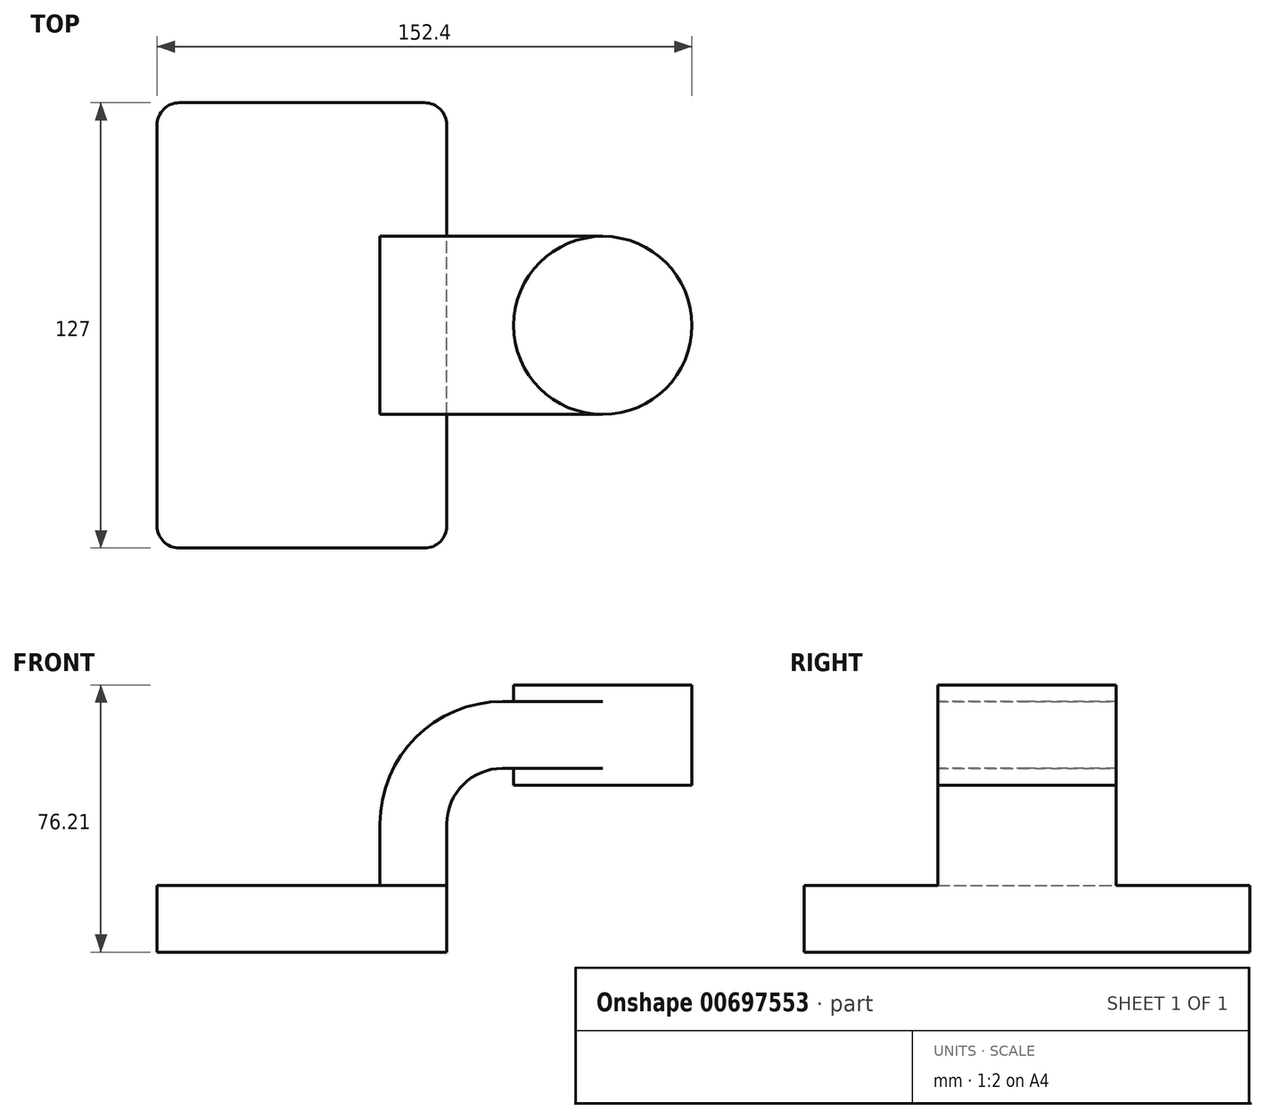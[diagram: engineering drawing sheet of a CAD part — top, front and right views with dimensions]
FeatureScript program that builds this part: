
annotation { "Feature Type Name" : "Feature", "Feature Type Description" : "" }
export const myFeature = defineFeature(function(context is Context, id is Id, definition is map)
    precondition{}
    {
        {
            var Q0;
            Q0=qCreatedBy(makeId("Front.planeOp"),FACE);
            var sketch = newSketch(context, id + "F0", { "sketchPlane" : qUnion([Q0])});
            skLineSegment(sketch, "E0.bottom", {"start": v(-41.28, -9.52) * mm, "end": v(41.28, -9.52) * mm});
            skLineSegment(sketch, "E0.top", {"start": v(-41.28, 9.53) * mm, "end": v(41.28, 9.53) * mm});
            skLineSegment(sketch, "E0.left", {"start": v(-41.28, -9.52) * mm, "end": v(-41.28, 9.53) * mm});
            skLineSegment(sketch, "E0.right", {"start": v(41.28, -9.52) * mm, "end": v(41.28, 9.53) * mm});
            skPoint(sketch, "E0.middle", {"position": v(0, 0) * mm});
            skLineSegment(sketch, "E1.bottom", {"start": v(60.32, 38.1) * mm, "end": v(111.13, 38.1) * mm});
            skLineSegment(sketch, "E1.top", {"start": v(60.32, 66.68) * mm, "end": v(111.12, 66.68) * mm});
            skLineSegment(sketch, "E1.left", {"start": v(60.32, 38.1) * mm, "end": v(60.32, 66.68) * mm});
            skLineSegment(sketch, "E1.right", {"start": v(111.13, 38.1) * mm, "end": v(111.13, 66.68) * mm});
            skPoint(sketch, "E1.middle", {"position": v(85.72, 52.39) * mm});
            skLineSegment(sketch, "E2", {"start": v(41.27, 9.53) * mm, "end": v(41.27, 27) * mm});
            skArc(sketch, "E3", {"start": v(41.27, 27) * mm, "mid": v(45.92, 38.23) * mm, "end": v(57.15, 42.88) * mm});
            skLineSegment(sketch, "E4", {"start": v(57.15, 42.88) * mm, "end": v(85.72, 42.88) * mm});
            skLineSegment(sketch, "E5.0", {"start": v(57.15, 61.93) * mm, "end": v(85.72, 61.93) * mm});
            skArc(sketch, "E5.1", {"start": v(22.22, 27) * mm, "mid": v(32.45, 51.7) * mm, "end": v(57.15, 61.93) * mm});
            skLineSegment(sketch, "E5.2", {"start": v(22.22, 9.53) * mm, "end": v(22.22, 27) * mm});
            skLineSegment(sketch, "E6", {"start": v(85.72, 38.1) * mm, "end": v(85.72, 66.68) * mm});
            skFitSpline(sketch, "E7", {"points": [v(-41.27, 9.52) * mm, v(57.15, 61.93) * mm], "startDerivative": vector(0, 59.37) * mm, "endDerivative": vector(123, 0) * mm});
            skSolve(sketch);
        }
        {
            var Q0;
            Q0=makeQuery(id+"F0.imprint","IMPRINT",FACE,{"disambiguationData":[TD([[makeQuery(id+"F0.imprint","IMPRINT",EDGE,{"derivedFrom":sQuery(id+"F0.wireOp",EDGE,"E0.bottom")}),1.0]])]});
            extrude(context, id + "F1", {"entities" : qUnion([Q0]), "endBound" : BoundingType.SYMMETRIC, "depth" : 127 * mm, "offsetDistance" : 25.4 * mm});
        }
        {
            var Q0;
            {var subQ1=sQuery(id+"F0.wireOp",EDGE,"E2");Q0=makeQuery(id+"F0.imprint","IMPRINT",FACE,{"disambiguationData":[TD([[makeQuery(id+"F0.imprint","IMPRINT",EDGE,{"derivedFrom":subQ1}),1.0]])]});}
            var Q1;
            {var subQ0=sQuery(id+"F0.wireOp",EDGE,"E4");var subQ1=sQuery(id+"F0.wireOp",EDGE,"E1.left");var subQ2=makeQuery(id+"F0.imprint","INTERSECT",VERTEX,{"derivedFrom":[subQ1,subQ0]});Q1=makeQuery(id+"F0.imprint","IMPRINT",FACE,{"disambiguationData":[TD([[makeQuery(id+"F0.imprint","IMPRINT",EDGE,{"disambiguationData":[TD([[subQ2,-1.0]])],"derivedFrom":subQ1}),-1.0]])]});}
            extrude(context, id + "F2", {"entities" : qUnion([Q0, Q1]), "operationType" : NewBodyOperationType.ADD, "endBound" : BoundingType.SYMMETRIC, "depth" : 50.8 * mm, "offsetDistance" : 25.4 * mm});
        }
        {
            var Q0;
            Q0=makeQuery(id+"F0.imprint","IMPRINT",FACE,{"disambiguationData":[TD([[makeQuery(id+"F0.imprint","IMPRINT",EDGE,{"derivedFrom":sQuery(id+"F0.wireOp",EDGE,"E5.1")}),1.0]])]});
            extrude(context, id + "F3", {"entities" : qUnion([Q0]), "operationType" : NewBodyOperationType.ADD, "endBound" : BoundingType.SYMMETRIC, "depth" : 15.88 * mm, "offsetDistance" : 25.4 * mm});
        }
        {
            var Q0;
            {var subQ0=sQuery(id+"F0.wireOp",EDGE,"E1.right");Q0=makeQuery(id+"F0.imprint","IMPRINT",FACE,{"disambiguationData":[TD([[makeQuery(id+"F0.imprint","IMPRINT",EDGE,{"derivedFrom":subQ0}),1.0]])]});}
            var Q1;
            Q1=sQuery(id+"F0.wireOp",EDGE,"E6");
            revolve(context, id + "F4", {"operationType" : NewBodyOperationType.ADD, "entities" : qUnion([Q0]), "axis" : qUnion([Q1]), "revolveType" : RevolveType.FULL});
        }
        {
            var Q0;
            Q0=makeQuery(id+"F1.opExtrude","CAP_EDGE",EDGE,{"disambiguationData":[OSD([sQuery(id+"F0.wireOp",EDGE,"E0.right")])],"isStart":false});
            var Q1;
            Q1=makeQuery(id+"F1.opExtrude","CAP_EDGE",EDGE,{"disambiguationData":[OSD([sQuery(id+"F0.wireOp",EDGE,"E0.left")])],"isStart":false});
            var Q2;
            Q2=makeQuery(id+"F1.opExtrude","CAP_EDGE",EDGE,{"disambiguationData":[OSD([sQuery(id+"F0.wireOp",EDGE,"E0.left")])],"isStart":true});
            var Q3;
            Q3=makeQuery(id+"F1.opExtrude","CAP_EDGE",EDGE,{"disambiguationData":[OSD([sQuery(id+"F0.wireOp",EDGE,"E0.right")])],"isStart":true});
            fillet(context, id + "F5", {"entities" : qUnion([Q0, Q1, Q2, Q3]), "radius" : 6.35 * mm, "tangentPropagation" : true, "allowEdgeOverflow" : false});
        }
    });
